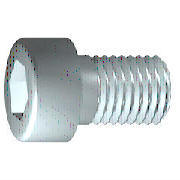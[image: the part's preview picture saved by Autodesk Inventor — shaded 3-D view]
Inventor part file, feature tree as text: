
AUTODESK INVENTOR PART (.ipt)
format: ipt  version: 2025 (Build 290162010, 162A)  size: 187,904 bytes
history: native  units: mm (DEFAULTED — no unit token found)
features: extrude x1, plane x1, fillet x1
ambient origin geometry x7: Origin, YZ Plane, XY Plane, X Axis, Y Axis, Z Axis, Center Point
bodies: Solid1 (feature_tree), Body (feature_tree)
feature tree (3):
  extrude  "Slot"  Depth=18.75mm
  plane  "Work Plane1"
  fillet  "Fillet2"  Radius=0.306825mm
